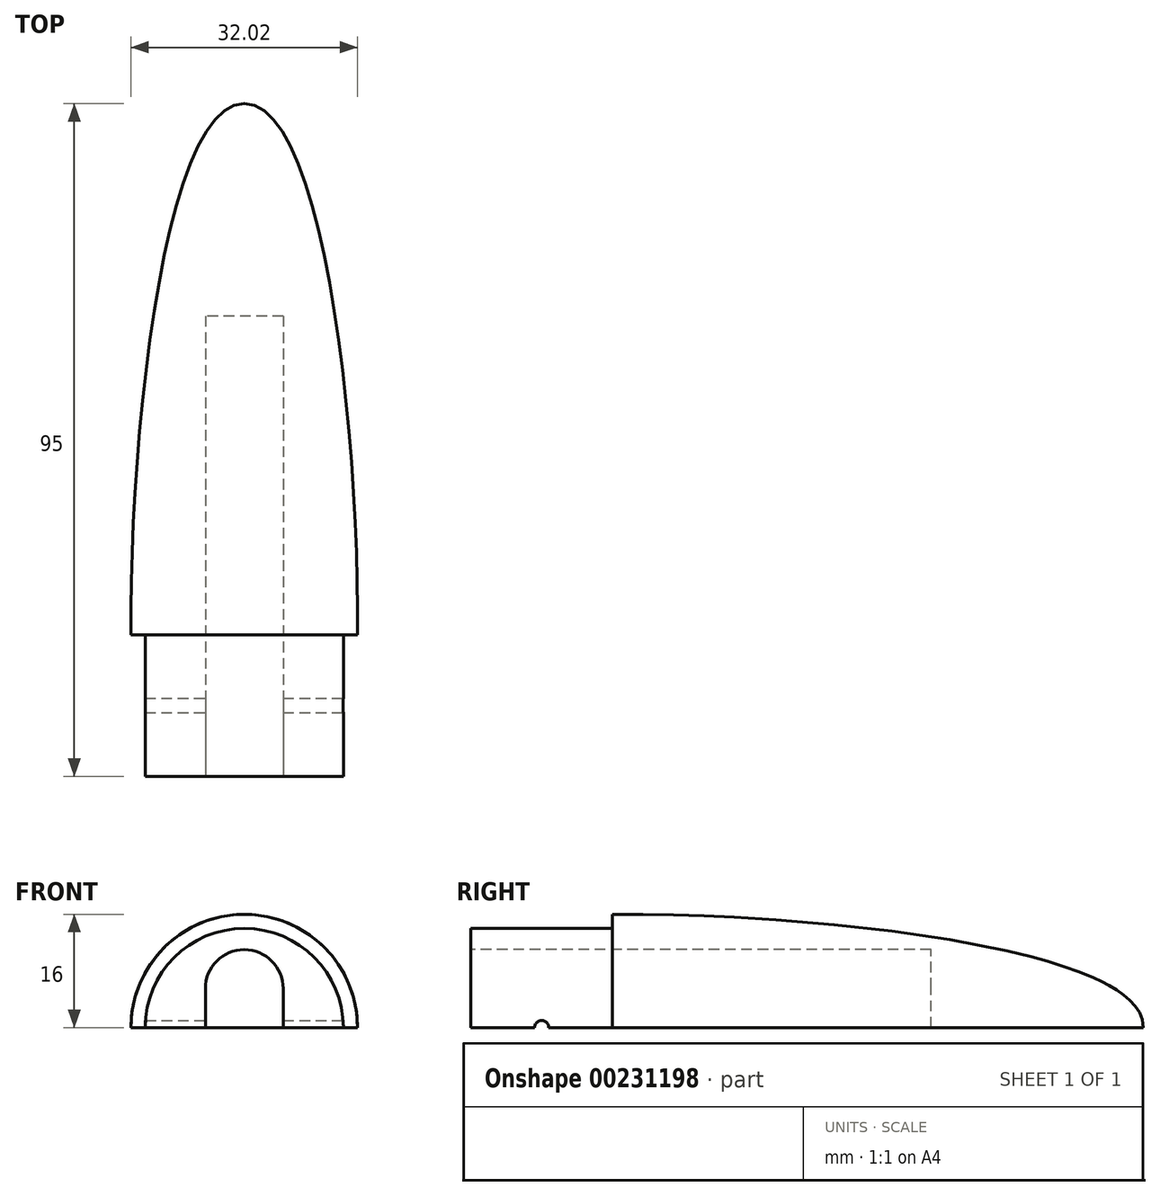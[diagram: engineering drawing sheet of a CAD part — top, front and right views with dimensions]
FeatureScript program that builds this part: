
annotation { "Feature Type Name" : "Feature", "Feature Type Description" : "" }
export const myFeature = defineFeature(function(context is Context, id is Id, definition is map)
    precondition{}
    {
        {
            var Q0;
            Q0=qCreatedBy(makeId("Top.planeOp"),FACE);
            var sketch = newSketch(context, id + "F0", { "sketchPlane" : qUnion([Q0])});
            skLineSegment(sketch, "E0.bottom", {"start": v(-5.5, 65) * mm, "end": v(5.5, 65) * mm});
            skLineSegment(sketch, "E0.top", {"start": v(-5.5, 20) * mm, "end": v(5.5, 20) * mm});
            skLineSegment(sketch, "E0.left", {"start": v(-5.5, 65) * mm, "end": v(-5.5, 20) * mm});
            skLineSegment(sketch, "E0.right", {"start": v(5.5, 65) * mm, "end": v(5.5, 20) * mm});
            skLineSegment(sketch, "E1", {"start": v(0, 0) * mm, "end": v(14, 0) * mm});
            skLineSegment(sketch, "E2", {"start": v(0, 0) * mm, "end": v(-14, 0) * mm});
            skLineSegment(sketch, "E3", {"start": v(-14, 0) * mm, "end": v(-14, 20) * mm});
            skLineSegment(sketch, "E4", {"start": v(-14, 20) * mm, "end": v(14, 20) * mm});
            skLineSegment(sketch, "E5", {"start": v(14, 20) * mm, "end": v(14, 0) * mm});
            skLineSegment(sketch, "E6", {"start": v(-5.5, 20) * mm, "end": v(-5.5, 0) * mm});
            skLineSegment(sketch, "E7", {"start": v(5.5, 20) * mm, "end": v(5.5, 0) * mm});
            skLineSegment(sketch, "E8", {"start": v(14, 20) * mm, "end": v(16, 20) * mm});
            skLineSegment(sketch, "E9", {"start": v(-14, 20) * mm, "end": v(-16, 20) * mm});
            skLineSegment(sketch, "E10", {"start": v(0, 20) * mm, "end": v(0, 95) * mm});
            skFitSpline(sketch, "E11", {"points": [v(0, 95) * mm, v(16, 20) * mm], "startDerivative": vector(34.31, 0.3) * mm, "endDerivative": vector(-0.78, -82.14) * mm});
            skFitSpline(sketch, "E12.MirrorCS", {"points": [v(0, 95) * mm, v(-16, 20) * mm], "startDerivative": vector(-34.31, 0.3) * mm, "endDerivative": vector(0.78, -82.14) * mm});
            skSolve(sketch);
        }
        {
            var Q0;
            Q0=qCreatedBy(makeId("Front.planeOp"),FACE);
            var sketch = newSketch(context, id + "F1", { "sketchPlane" : qUnion([Q0])});
            skLineSegment(sketch, "E13", {"start": v(0, 0) * mm, "end": v(0, 14.5) * mm});
            skCircle(sketch, "E14", {"center": v(0, 0) * mm, "radius": 14.5 * mm});
            skLineSegment(sketch, "E15", {"start": v(0, 0) * mm, "end": v(5.5, 0) * mm});
            skLineSegment(sketch, "E16", {"start": v(5.5, 0) * mm, "end": v(5.5, 5.5) * mm});
            skLineSegment(sketch, "E17", {"start": v(5.5, 5.5) * mm, "end": v(0, 5.5) * mm});
            skCircle(sketch, "E18", {"center": v(0, 5.5) * mm, "radius": 5.5 * mm});
            skLineSegment(sketch, "E19", {"start": v(0, 0) * mm, "end": v(-5.5, 0) * mm});
            skLineSegment(sketch, "E20", {"start": v(-5.5, 0) * mm, "end": v(-5.5, 5.5) * mm});
            skLineSegment(sketch, "E21", {"start": v(-5.5, 5.5) * mm, "end": v(0, 5.5) * mm});
            skSolve(sketch);
        }
        {
            var Q0;
            {var subQ1=sQuery(id+"F0.wireOp",EDGE,"E0.right");Q0=makeQuery(id+"F0.imprint","IMPRINT",FACE,{"disambiguationData":[TD([[makeQuery(id+"F0.imprint","IMPRINT",EDGE,{"derivedFrom":subQ1}),1.0]])]});}
            var Q1;
            {var subQ0=sQuery(id+"F0.wireOp",EDGE,"E5");Q1=makeQuery(id+"F0.imprint","IMPRINT",FACE,{"disambiguationData":[TD([[makeQuery(id+"F0.imprint","IMPRINT",EDGE,{"derivedFrom":subQ0}),-1.0]])]});}
            var Q2;
            Q2=sQuery(id+"F0.wireOp",EDGE,"E10");
            revolve(context, id + "F2", {"entities" : qUnion([Q0, Q1]), "axis" : qUnion([Q2]), "revolveType" : RevolveType.ONE_DIRECTION, "oppositeDirection" : true, "angle" : 180 * degree});
        }
        {
            var Q0;
            {var subQ3=sQuery(id+"F1.wireOp",EDGE,"E17");Q0=makeQuery(id+"F1.imprint","IMPRINT",FACE,{"disambiguationData":[TD([[makeQuery(id+"F1.imprint","IMPRINT",EDGE,{"derivedFrom":subQ3}),1.0]])]});}
            var Q1;
            {var subQ0=sQuery(id+"F1.wireOp",EDGE,"E15");Q1=makeQuery(id+"F1.imprint","IMPRINT",FACE,{"disambiguationData":[TD([[makeQuery(id+"F1.imprint","IMPRINT",EDGE,{"derivedFrom":subQ0}),1.0]])]});}
            var Q2;
            {var subQ0=sQuery(id+"F1.wireOp",EDGE,"E19");Q2=makeQuery(id+"F1.imprint","IMPRINT",FACE,{"disambiguationData":[TD([[makeQuery(id+"F1.imprint","IMPRINT",EDGE,{"derivedFrom":subQ0}),-1.0]])]});}
            var Q3;
            {var subQ3=sQuery(id+"F1.wireOp",EDGE,"E21");Q3=makeQuery(id+"F1.imprint","IMPRINT",FACE,{"disambiguationData":[TD([[makeQuery(id+"F1.imprint","IMPRINT",EDGE,{"derivedFrom":subQ3}),-1.0]])]});}
            var Q4;
            {var subQ0=sQuery(id+"F1.wireOp",EDGE,"E21");Q4=makeQuery(id+"F1.imprint","IMPRINT",FACE,{"disambiguationData":[TD([[makeQuery(id+"F1.imprint","IMPRINT",EDGE,{"derivedFrom":subQ0}),1.0]])]});}
            var Q5;
            {var subQ0=sQuery(id+"F1.wireOp",EDGE,"E17");Q5=makeQuery(id+"F1.imprint","IMPRINT",FACE,{"disambiguationData":[TD([[makeQuery(id+"F1.imprint","IMPRINT",EDGE,{"derivedFrom":subQ0}),-1.0]])]});}
            extrude(context, id + "F3", {"entities" : qUnion([Q0, Q1, Q2, Q3, Q4, Q5]), "operationType" : NewBodyOperationType.REMOVE, "oppositeDirection" : true, "depth" : 65 * mm});
        }
        {
            var Q0;
            Q0=qCreatedBy(makeId("Right.planeOp"),FACE);
            cPlane(context, id + "F4", {"entities" : qUnion([Q0]), "cplaneType" : CPlaneType.OFFSET, "offset" : 14 * mm, "width" : 150 * mm, "height" : 150 * mm});
        }
        {
            var Q0;
            Q0=qCreatedBy(id+"F4.planeOp",FACE);
            var sketch = newSketch(context, id + "F5", { "sketchPlane" : qUnion([Q0])});
            skCircle(sketch, "E22", {"center": v(10, 0) * mm, "radius": 1 * mm});
            skSolve(sketch);
        }
        {
            var Q0;
            Q0=makeQuery(id+"F5.imprint","IMPRINT",FACE,{"disambiguationData":[TD([[makeQuery(id+"F5.imprint","IMPRINT",EDGE,{"derivedFrom":sQuery(id+"F5.wireOp",EDGE,"E22")}),1.0]])]});
            extrude(context, id + "F6", {"entities" : qUnion([Q0]), "operationType" : NewBodyOperationType.REMOVE, "oppositeDirection" : true, "depth" : 28 * mm});
        }
    });
